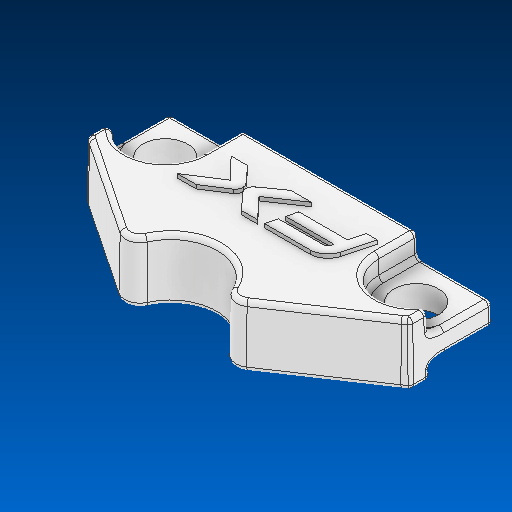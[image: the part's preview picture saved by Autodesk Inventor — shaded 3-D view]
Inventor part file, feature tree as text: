
AUTODESK INVENTOR PART (.ipt)
format: ipt  version: 2022.2 (Build 262287000, 287)  size: 473,088 bytes
history: native  units: in
note: dims shown in document units (in); Inventor stores cm internally (conversion verified against a paired STEP export)
features: fillet x1
ambient origin geometry x8: Origin, YZ Plane, XZ Plane, XY Plane, X Axis, Y Axis, Z Axis, Center Point
bodies: Solid1 (feature_tree)
feature tree (1):
  fillet  "Fillet3"  [1 undecoded]
note: 1 required parameter value undecoded (feature->parameter linkage not recoverable at this tier; creation-order binding heuristic only, values carry confidence <= 0.55)
